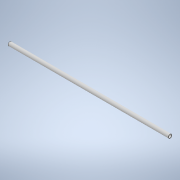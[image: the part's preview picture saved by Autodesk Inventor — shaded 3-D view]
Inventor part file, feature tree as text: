
AUTODESK INVENTOR PART (.ipt)
format: ipt  version: 2022 (Build 260153000, 153)  size: 100,864 bytes
history: native  units: in
note: dims shown in document units (in); Inventor stores cm internally (conversion verified against a paired STEP export)
features: extrude x1
ambient origin geometry x8: Origin, YZ Plane, XZ Plane, XY Plane, X Axis, Y Axis, Z Axis, Center Point
bodies: Solid1 (feature_tree)
feature tree (1):
  extrude  "Extrude1"  [1 undecoded]
note: 1 required parameter value undecoded (feature->parameter linkage not recoverable at this tier; creation-order binding heuristic only, values carry confidence <= 0.55)
